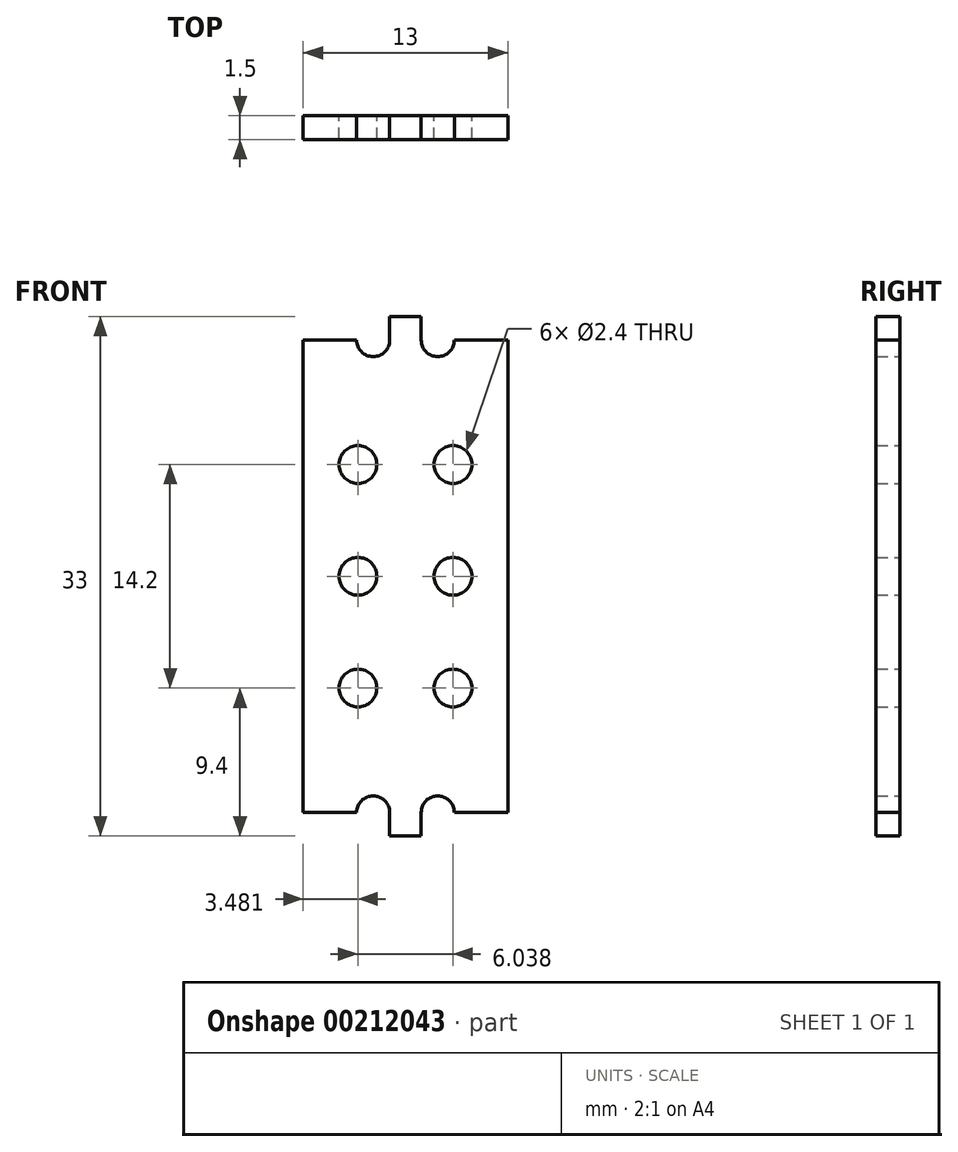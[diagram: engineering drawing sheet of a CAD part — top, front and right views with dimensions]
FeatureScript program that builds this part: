
annotation { "Feature Type Name" : "Feature", "Feature Type Description" : "" }
export const myFeature = defineFeature(function(context is Context, id is Id, definition is map)
    precondition{}
    {
        {
            var Q0;
            Q0=qCreatedBy(makeId("Front.planeOp"),FACE);
            var sketch = newSketch(context, id + "F0", { "sketchPlane" : qUnion([Q0])});
            skLineSegment(sketch, "E0.bottom", {"start": v(-3.1, 15) * mm, "end": v(-6.5, 15) * mm});
            skLineSegment(sketch, "E0.right", {"start": v(-6.5, 15) * mm, "end": v(-6.5, 0) * mm});
            skLineSegment(sketch, "E1.right", {"start": v(-1, 15) * mm, "end": v(-1, 16.5) * mm});
            skLineSegment(sketch, "E2.MirrorCS", {"start": v(6.5, 15) * mm, "end": v(6.5, 0) * mm});
            skLineSegment(sketch, "E3.MirrorCS", {"start": v(1, 15) * mm, "end": v(1, 16.5) * mm});
            skLineSegment(sketch, "E4.MirrorCS", {"start": v(3.1, 15) * mm, "end": v(6.5, 15) * mm});
            skPoint(sketch, "E0.left.start.orphan", {"position": v(0, 15) * mm});
            skCircle(sketch, "E5.MirrorC", {"center": v(3.02, 7.1) * mm, "radius": 1.2 * mm});
            skCircle(sketch, "E6.MirrorC", {"center": v(3.02, 0) * mm, "radius": 1.2 * mm});
            skArc(sketch, "E7", {"start": v(1, 15) * mm, "mid": v(2.05, 13.95) * mm, "end": v(3.1, 15) * mm});
            skArc(sketch, "E8", {"start": v(-3.1, 15) * mm, "mid": v(-2.05, 13.95) * mm, "end": v(-1, 15) * mm});
            skLineSegment(sketch, "E9", {"start": v(0, 0) * mm, "end": v(9.79, 0) * mm, "construction": true});
            skLineSegment(sketch, "E10", {"start": v(0, 0) * mm, "end": v(0, 23.02) * mm, "construction": true});
            skLineSegment(sketch, "E11", {"start": v(-1, 16.5) * mm, "end": v(1, 16.5) * mm});
            skLineSegment(sketch, "E12", {"start": v(0, 0) * mm, "end": v(-12.41, 0) * mm, "construction": true});
            skPoint(sketch, "E12.endSnap0", {"position": v(-6.5, 0) * mm});
            skLineSegment(sketch, "E13.MirrorCS", {"start": v(6.5, -15) * mm, "end": v(6.5, 0) * mm});
            skLineSegment(sketch, "E14.MirrorCS", {"start": v(-6.5, -15) * mm, "end": v(-6.5, 0) * mm});
            skLineSegment(sketch, "E15.MirrorCS", {"start": v(1, -15) * mm, "end": v(1, -16.5) * mm});
            skLineSegment(sketch, "E16.MirrorCS", {"start": v(-1, -15) * mm, "end": v(-1, -16.5) * mm});
            skPoint(sketch, "E17.MirrorP", {"position": v(0, -15) * mm});
            skLineSegment(sketch, "E18.MirrorCS", {"start": v(3.1, -15) * mm, "end": v(6.5, -15) * mm});
            skLineSegment(sketch, "E19.MirrorCS", {"start": v(-3.1, -15) * mm, "end": v(-6.5, -15) * mm});
            skLineSegment(sketch, "E20.MirrorCS", {"start": v(-1, -16.5) * mm, "end": v(1, -16.5) * mm});
            skArc(sketch, "E21.MirrorCS", {"start": v(-3.1, -15) * mm, "mid": v(-2.05, -13.95) * mm, "end": v(-1, -15) * mm});
            skArc(sketch, "E22.MirrorCS", {"start": v(1, -15) * mm, "mid": v(2.05, -13.95) * mm, "end": v(3.1, -15) * mm});
            skLineSegment(sketch, "E23", {"start": v(3.02, 11.59) * mm, "end": v(3.02, -11.22) * mm, "construction": true});
            skCircle(sketch, "E24.MirrorC", {"center": v(3.02, -7.1) * mm, "radius": 1.2 * mm});
            skCircle(sketch, "E25.MirrorC", {"center": v(-3.02, -7.1) * mm, "radius": 1.2 * mm});
            skCircle(sketch, "E26.MirrorC", {"center": v(-3.02, 0) * mm, "radius": 1.2 * mm});
            skCircle(sketch, "E27.MirrorC", {"center": v(-3.02, 7.1) * mm, "radius": 1.2 * mm});
            skSolve(sketch);
        }
        {
            var Q0;
            Q0 = qSketchRegion(id + "F0", true);
            extrude(context, id + "F1", {"entities" : qUnion([Q0]), "depth" : 1.5 * mm});
        }
    });
